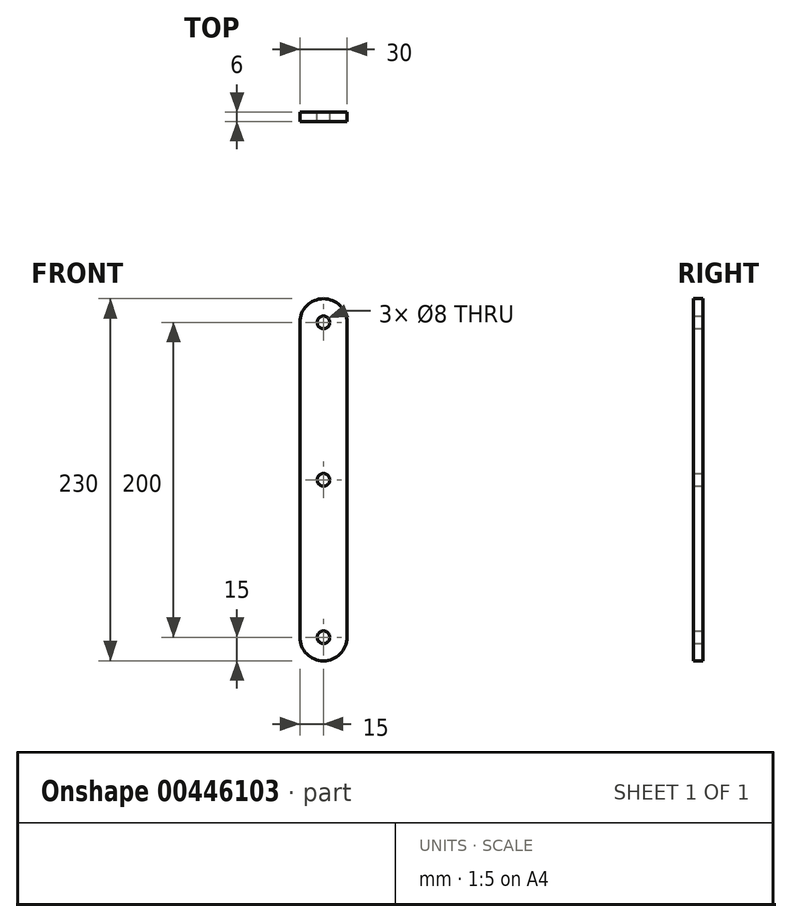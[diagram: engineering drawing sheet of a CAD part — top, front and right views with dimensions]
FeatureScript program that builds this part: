
annotation { "Feature Type Name" : "Feature", "Feature Type Description" : "" }
export const myFeature = defineFeature(function(context is Context, id is Id, definition is map)
    precondition{}
    {
        {
            var Q0;
            Q0=qCreatedBy(makeId("Front.planeOp"),FACE);
            var sketch = newSketch(context, id + "F0", { "sketchPlane" : qUnion([Q0])});
            skLineSegment(sketch, "E0", {"start": v(0, 200) * mm, "end": v(0, 0) * mm});
            skLineSegment(sketch, "E1", {"start": v(30, 200) * mm, "end": v(30, 0) * mm});
            skArc(sketch, "E2", {"start": v(0, 200) * mm, "mid": v(15, 215) * mm, "end": v(30, 200) * mm});
            skArc(sketch, "E3", {"start": v(30, 0) * mm, "mid": v(15, -15) * mm, "end": v(0, 0) * mm});
            skCircle(sketch, "E4", {"center": v(15, 200) * mm, "radius": 4 * mm});
            skCircle(sketch, "E5", {"center": v(15, 0) * mm, "radius": 4 * mm});
            skCircle(sketch, "E6", {"center": v(15, 100) * mm, "radius": 4 * mm});
            skPoint(sketch, "E6.centerSnap0", {"position": v(0, 100) * mm});
            skLineSegment(sketch, "E7", {"start": v(0, 100) * mm, "end": v(30, 100) * mm, "construction": true});
            skSolve(sketch);
        }
        {
            var Q0;
            Q0 = qSketchRegion(id + "F0", true);
            extrude(context, id + "F1", {"entities" : qUnion([Q0]), "depth" : 6 * mm});
        }
    });
